# Revit family: MP305
name_source: partatom
category: Generic Models
units: mm (PartAtom-declared; Revit-internal decimal feet)

## family parameters
Always vertical = No
Can host rebar = No
Cut with Voids When Loaded = No
Part Type = Normal
Room Calculation Point = No
Round Connector Dimension = Use Diameter
Shared = No
Work Plane-Based = Yes

## types (1)
- NBS Standard Parameters
    AssetType = Fixed
    BIMObjectName = Metpro_metprolibrary_channelcablesupports_channelbracket
    Color = Black
    Default Elevation = 1219 mm
    Description = MP305 - H Frame Kit
    DurationUnit = 1 Year
    Features = SWL 350kg, Kit includes 2 x feet & 1 x Fixing Kit
    Finish = Foot - Black / Brackets & Fixings - HDG
    Keynote = SWL Loading 350kg
    Manufacturer = Metpro Ltd
    ManufacturerName = Metpro ltd
    ManufacturerURL = www.metpro.co.uk
    Material = Foot - HDPE / Brackets & Fixings - Carbon Steel
    ModelNumber = MP305
    ModelReference = Channel Cable Supports
    NBSDescription = Channel Cable Supports
    NBSReference = 90-55-10/305
    Name = MP305 - H FRAME KIT
    NominalHeight = 122 mm  [stored 0.400262 ft]
    NominalLength = 305 mm  [stored 1.00066 ft]
    NominalWidth = 305 mm  [stored 1.00066 ft]
    ProductInformation = www.metpro.co.uk/pdf/MP305.pdf
    Shape = Square
    Size = 305mm
    URL = www.metpro.co.uk
    Uniclass2 = Pr_65_70_11_19
    Version = 1
    WarrantyDurationUnit = 12 Months
    WarrantyGuarantorParts = 12 Months
    Weight = 3.4

note: [stored X ft] marks values corroborated as IEEE doubles in the binary element streams (Revit-internal decimal feet)

## geometry (parser evidence)
native form markers: Sweep x2
no freeform markers — native parametric forms only
